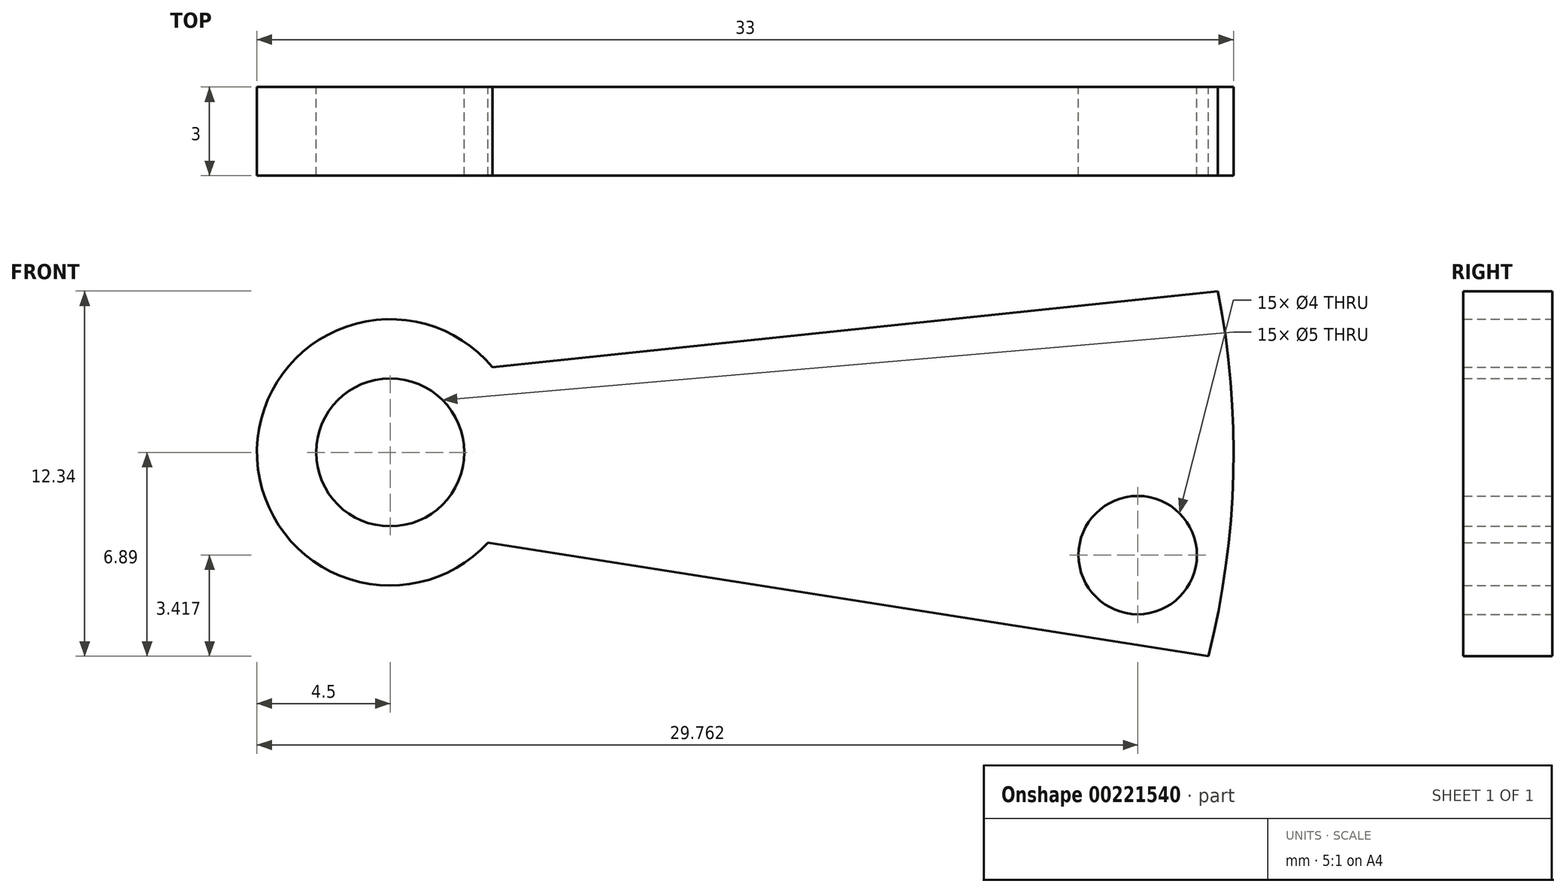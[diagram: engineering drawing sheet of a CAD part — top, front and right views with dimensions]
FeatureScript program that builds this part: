
annotation { "Feature Type Name" : "Feature", "Feature Type Description" : "" }
export const myFeature = defineFeature(function(context is Context, id is Id, definition is map)
    precondition{}
    {
        {
            var Q0;
            Q0=qCreatedBy(makeId("Front.planeOp"),FACE);
            var sketch = newSketch(context, id + "F0", { "sketchPlane" : qUnion([Q0])});
            skCircle(sketch, "E0", {"center": v(0, 0) * mm, "radius": 2.5 * mm});
            skCircle(sketch, "E1", {"center": v(0, 0) * mm, "radius": 4.5 * mm});
            skArc(sketch, "E2", {"start": v(27.66, -6.89) * mm, "mid": v(28.5, -0.74) * mm, "end": v(27.97, 5.45) * mm});
            skLineSegment(sketch, "E3", {"start": v(27.97, 5.45) * mm, "end": v(0, 0) * mm, "construction": true});
            skLineSegment(sketch, "E4", {"start": v(0, 0) * mm, "end": v(27.66, -6.89) * mm, "construction": true});
            skCircle(sketch, "E5", {"center": v(25.26, -3.47) * mm, "radius": 3 * mm, "construction": true});
            skCircle(sketch, "E6", {"center": v(25.26, -3.47) * mm, "radius": 2 * mm});
            skLineSegment(sketch, "E7", {"start": v(27.97, 5.45) * mm, "end": v(-0.26, 2.49) * mm});
            skLineSegment(sketch, "E8", {"start": v(27.66, -6.89) * mm, "end": v(-0.39, -2.47) * mm});
            skSolve(sketch);
        }
        {
            var Q0;
            {var subQ1=sQuery(id+"F0.wireOp",EDGE,"E2");Q0=makeQuery(id+"F0.imprint","IMPRINT",FACE,{"disambiguationData":[TD([[makeQuery(id+"F0.imprint","IMPRINT",EDGE,{"derivedFrom":subQ1}),1.0]])]});}
            var Q1;
            {var subQ0=sQuery(id+"F0.wireOp",EDGE,"E7");var subQ1=sQuery(id+"F0.wireOp",EDGE,"E0");var subQ2=makeQuery(id+"F0.imprint","INTERSECT",VERTEX,{"derivedFrom":[subQ1,subQ0]});Q1=makeQuery(id+"F0.imprint","IMPRINT",FACE,{"disambiguationData":[TD([[makeQuery(id+"F0.imprint","IMPRINT",EDGE,{"disambiguationData":[TD([[subQ2,-1.0]])],"derivedFrom":subQ1}),-1.0]])]});}
            var Q2;
            {var subQ0=sQuery(id+"F0.wireOp",EDGE,"E7");var subQ1=sQuery(id+"F0.wireOp",EDGE,"E0");var subQ2=makeQuery(id+"F0.imprint","INTERSECT",VERTEX,{"derivedFrom":[subQ1,subQ0]});Q2=makeQuery(id+"F0.imprint","IMPRINT",FACE,{"disambiguationData":[TD([[makeQuery(id+"F0.imprint","IMPRINT",EDGE,{"disambiguationData":[TD([[subQ2,1.0]])],"derivedFrom":subQ1}),-1.0]])]});}
            extrude(context, id + "F1", {"entities" : qUnion([Q0, Q1, Q2]), "depth" : 3 * mm});
        }
    });
